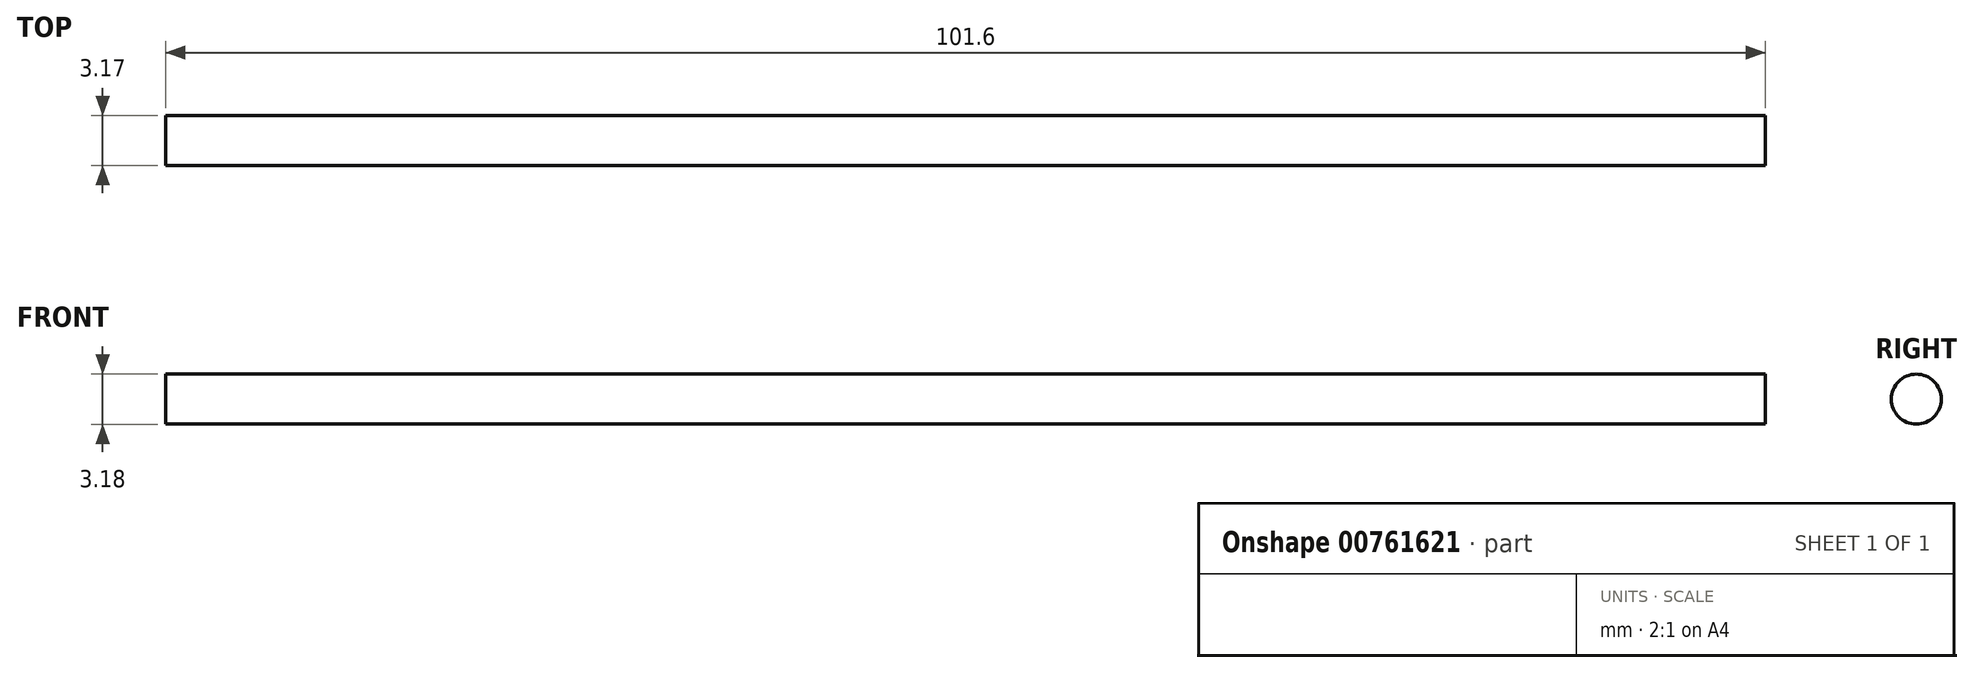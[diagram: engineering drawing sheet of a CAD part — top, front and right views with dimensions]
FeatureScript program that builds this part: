
annotation { "Feature Type Name" : "Feature", "Feature Type Description" : "" }
export const myFeature = defineFeature(function(context is Context, id is Id, definition is map)
    precondition{}
    {
        {
            var Q0;
            Q0=qCreatedBy(makeId("Right.planeOp"),FACE);
            var sketch = newSketch(context, id + "F0", { "sketchPlane" : qUnion([Q0])});
            skCircle(sketch, "E0", {"center": v(49.49, 0) * mm, "radius": 1.59 * mm});
            skSolve(sketch);
        }
        {
            var Q0;
            Q0=makeQuery(id+"F0.imprint","IMPRINT",FACE,{"disambiguationData":[TD([[makeQuery(id+"F0.imprint","IMPRINT",EDGE,{"derivedFrom":sQuery(id+"F0.wireOp",EDGE,"E0")}),1.0]])]});
            extrude(context, id + "F1", {"entities" : qUnion([Q0]), "depth" : 88.9 * mm, "offsetDistance" : 25.4 * mm, "hasSecondDirection" : true, "secondDirectionOppositeDirection" : true, "secondDirectionDepth" : 12.7 * mm});
        }
    });
